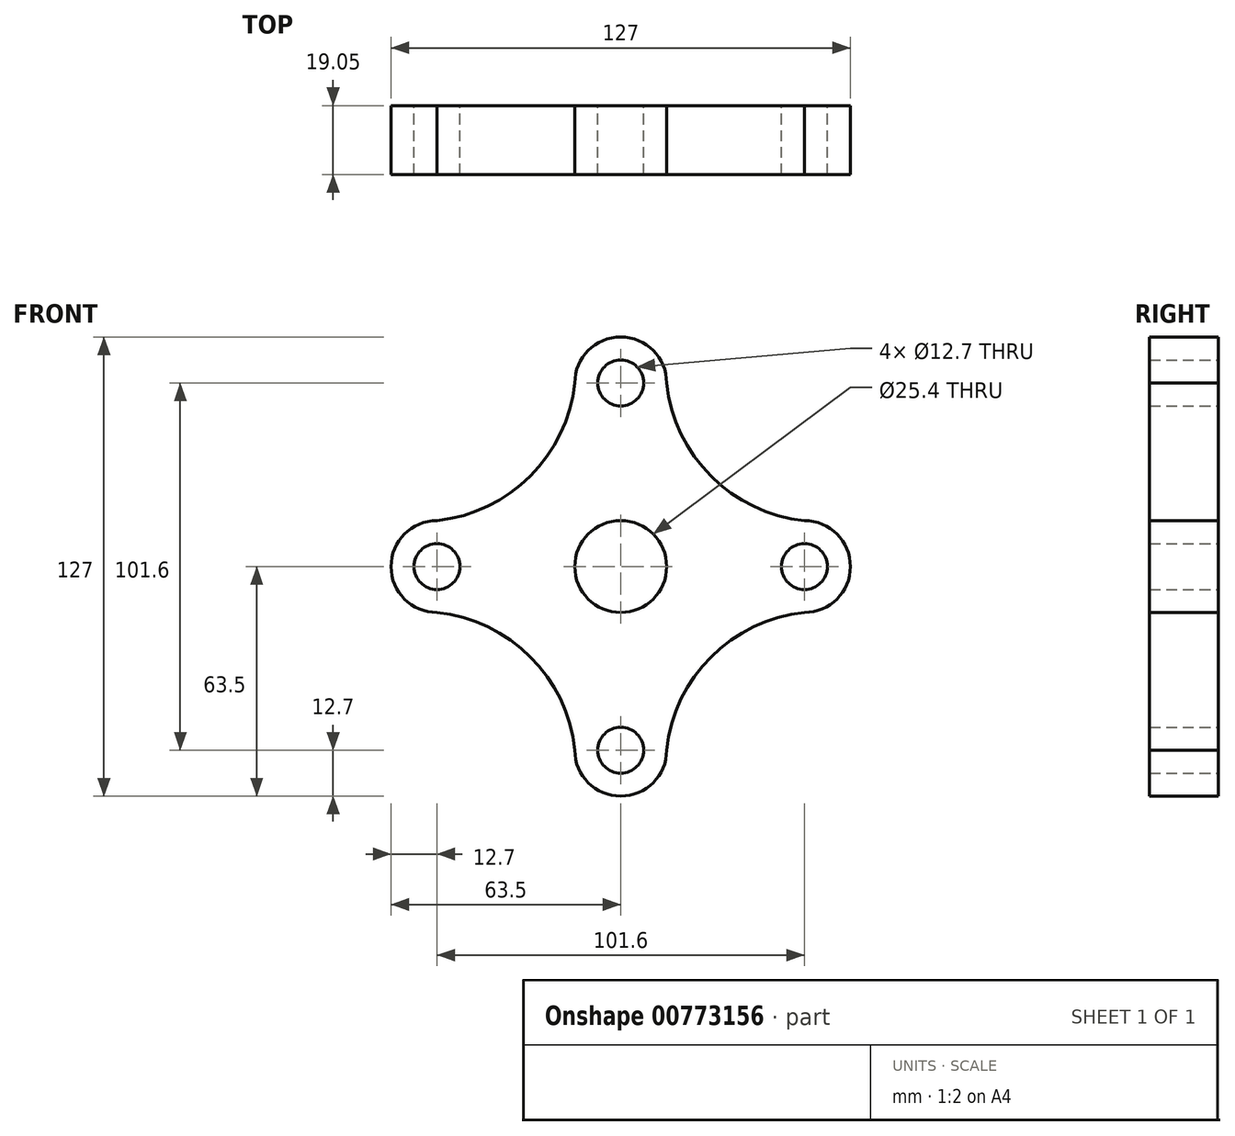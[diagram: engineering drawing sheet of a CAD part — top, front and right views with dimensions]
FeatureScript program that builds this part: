
annotation { "Feature Type Name" : "Feature", "Feature Type Description" : "" }
export const myFeature = defineFeature(function(context is Context, id is Id, definition is map)
    precondition{}
    {
        {
            var Q0;
            Q0=qCreatedBy(makeId("Front.planeOp"),FACE);
            var sketch = newSketch(context, id + "F0", { "sketchPlane" : qUnion([Q0])});
            skCircle(sketch, "E0", {"center": v(-101.6, 50.8) * mm, "radius": 6.35 * mm});
            skCircle(sketch, "E1", {"center": v(0, 50.8) * mm, "radius": 6.35 * mm});
            skCircle(sketch, "E2", {"center": v(-50.8, 50.8) * mm, "radius": 12.7 * mm});
            skCircle(sketch, "E3", {"center": v(-50.8, 0) * mm, "radius": 6.35 * mm});
            skCircle(sketch, "E4", {"center": v(-50.8, 101.6) * mm, "radius": 6.35 * mm});
            skArc(sketch, "E5", {"start": v(-101.6, 63.5) * mm, "mid": v(-75.83, 75.83) * mm, "end": v(-63.5, 101.6) * mm});
            skArc(sketch, "E6", {"start": v(-38.1, 101.6) * mm, "mid": v(-50.8, 114.3) * mm, "end": v(-63.5, 101.6) * mm});
            skArc(sketch, "E7", {"start": v(-101.6, 63.5) * mm, "mid": v(-114.3, 50.8) * mm, "end": v(-101.6, 38.1) * mm});
            skPoint(sketch, "E8.trimOffspring.end.orphan", {"position": v(-101.6, 101.6) * mm});
            skArc(sketch, "E9", {"start": v(-38.1, 101.6) * mm, "mid": v(-25.82, 75.78) * mm, "end": v(0, 63.5) * mm});
            skArc(sketch, "E10", {"start": v(0, 38.1) * mm, "mid": v(12.7, 50.8) * mm, "end": v(0, 63.5) * mm});
            skPoint(sketch, "E11.orphan", {"position": v(0, 101.6) * mm});
            skArc(sketch, "E12", {"start": v(0, 38.1) * mm, "mid": v(-25.82, 25.82) * mm, "end": v(-38.1, 0) * mm});
            skArc(sketch, "E13", {"start": v(-63.5, 0) * mm, "mid": v(-50.8, -12.7) * mm, "end": v(-38.1, 0) * mm});
            skArc(sketch, "E14", {"start": v(-63.5, 0) * mm, "mid": v(-75.78, 25.82) * mm, "end": v(-101.6, 38.1) * mm});
            skPoint(sketch, "E15.orphan", {"position": v(-101.6, 0) * mm});
            skPoint(sketch, "E16.orphan", {"position": v(0, 0) * mm});
            skSolve(sketch);
        }
        {
            var Q0;
            Q0=qSketchRegion(id+"F0",true);
            extrude(context, id + "F1", {"entities" : qUnion([Q0]), "depth" : 19.05 * mm});
        }
    });
